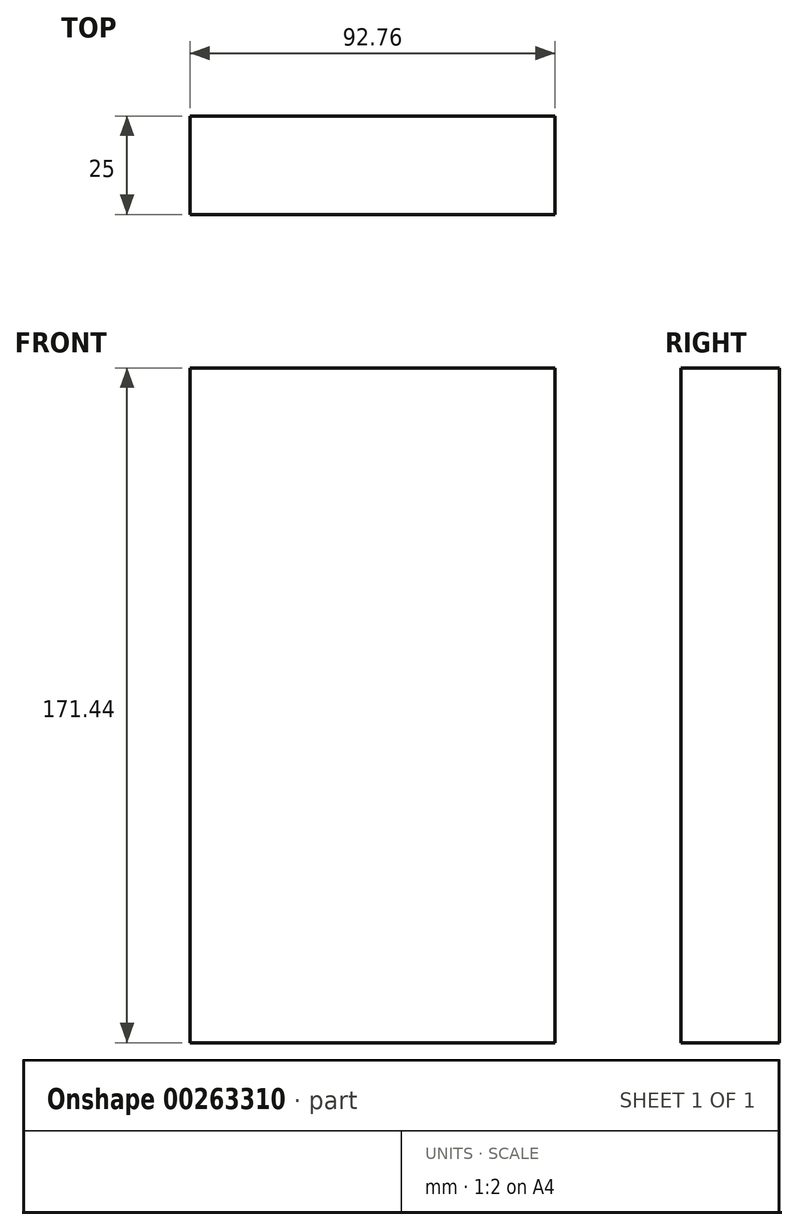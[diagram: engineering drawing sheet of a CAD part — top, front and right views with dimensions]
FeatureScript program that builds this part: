
annotation { "Feature Type Name" : "Feature", "Feature Type Description" : "" }
export const myFeature = defineFeature(function(context is Context, id is Id, definition is map)
    precondition{}
    {
        {
            var Q0;
            Q0=qCreatedBy(makeId("Front.planeOp"),FACE);
            var sketch = newSketch(context, id + "F0", { "sketchPlane" : qUnion([Q0])});
            skLineSegment(sketch, "E0.bottom", {"start": v(46.38, 85.72) * mm, "end": v(-46.38, 85.72) * mm});
            skLineSegment(sketch, "E0.top", {"start": v(46.38, -85.72) * mm, "end": v(-46.38, -85.72) * mm});
            skLineSegment(sketch, "E0.left", {"start": v(46.38, 85.72) * mm, "end": v(46.38, -85.72) * mm});
            skLineSegment(sketch, "E0.right", {"start": v(-46.38, 85.72) * mm, "end": v(-46.38, -85.72) * mm});
            skPoint(sketch, "E0.middle", {"position": v(0, 0) * mm});
            skSolve(sketch);
        }
        {
            var Q0;
            Q0=makeQuery(id+"F0.imprint","IMPRINT",FACE,{"disambiguationData":[TD([[makeQuery(id+"F0.imprint","IMPRINT",EDGE,{"derivedFrom":sQuery(id+"F0.wireOp",EDGE,"E0.bottom")}),1.0]])]});
            extrude(context, id + "F1", {"entities" : qUnion([Q0]), "depth" : 25 * mm});
        }
    });
